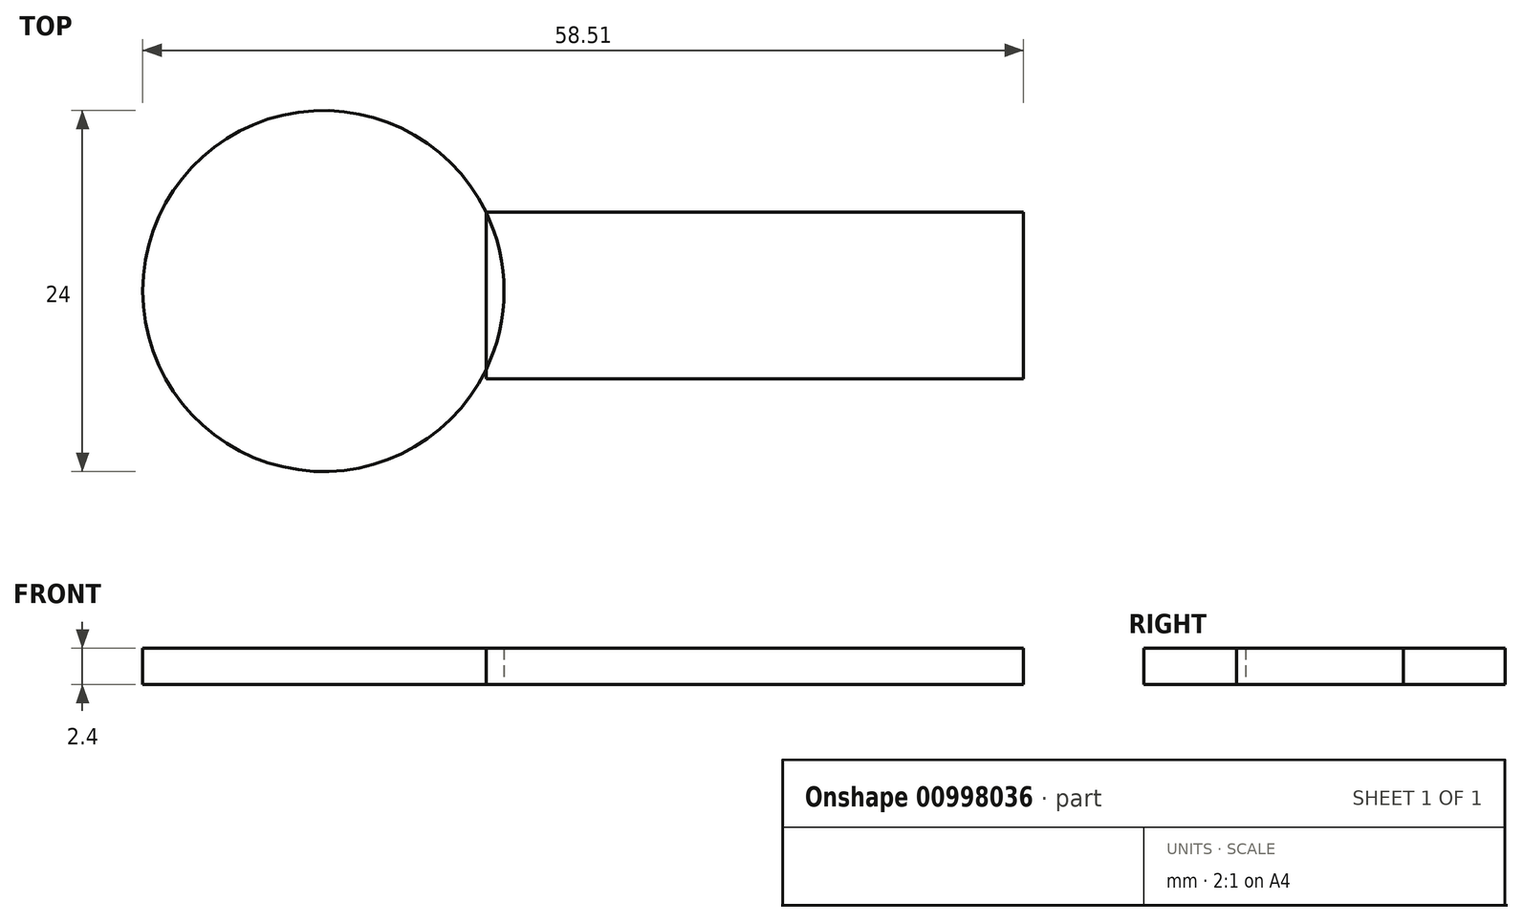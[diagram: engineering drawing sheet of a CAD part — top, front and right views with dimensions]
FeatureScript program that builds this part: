
annotation { "Feature Type Name" : "Feature", "Feature Type Description" : "" }
export const myFeature = defineFeature(function(context is Context, id is Id, definition is map)
    precondition{}
    {
        {
            var Q0;
            Q0=qCreatedBy(makeId("Top.planeOp"),FACE);
            var sketch = newSketch(context, id + "F0", { "sketchPlane" : qUnion([Q0])});
            skCircle(sketch, "E0", {"center": v(0, 0) * mm, "radius": 12 * mm});
            skLineSegment(sketch, "E1.bottom", {"start": v(10.8, 5.23) * mm, "end": v(46.51, 5.23) * mm});
            skLineSegment(sketch, "E1.top", {"start": v(10.8, -5.83) * mm, "end": v(46.51, -5.83) * mm});
            skLineSegment(sketch, "E1.left", {"start": v(10.8, 5.23) * mm, "end": v(10.8, -5.83) * mm});
            skLineSegment(sketch, "E1.right", {"start": v(46.51, 5.23) * mm, "end": v(46.51, -5.83) * mm});
            skSolve(sketch);
        }
        {
            var Q0;
            {var subQ0=sQuery(id+"F0.wireOp",EDGE,"E1.left");var subQ1=sQuery(id+"F0.wireOp",EDGE,"E0");var subQ3=makeQuery(id+"F0.imprint","INTERSECT",VERTEX,{"derivedFrom":[subQ1,subQ0]});Q0=makeQuery(id+"F0.imprint","IMPRINT",FACE,{"disambiguationData":[TD([[makeQuery(id+"F0.imprint","IMPRINT",EDGE,{"disambiguationData":[TD([[subQ3,1.0]])],"derivedFrom":subQ1}),1.0]])]});}
            var Q1;
            {var subQ4=sQuery(id+"F0.wireOp",EDGE,"E1.bottom");Q1=makeQuery(id+"F0.imprint","IMPRINT",FACE,{"disambiguationData":[TD([[makeQuery(id+"F0.imprint","IMPRINT",EDGE,{"derivedFrom":subQ4}),-1.0]])]});}
            extrude(context, id + "F1", {"entities" : qUnion([Q0, Q1]), "depth" : 2.4 * mm, "offsetDistance" : 25 * mm});
        }
    });
